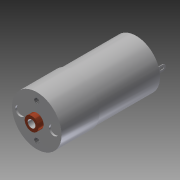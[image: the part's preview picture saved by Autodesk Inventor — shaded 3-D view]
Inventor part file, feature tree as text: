
AUTODESK INVENTOR PART (.ipt)
format: ipt  version: 2014 (Build 180170000, 170)  size: 193,536 bytes
history: native  units: in
note: dims shown in document units (in); Inventor stores cm internally (conversion verified against a paired STEP export)
features: sketch x11, extrude x10, hole x1
ambient origin geometry x8: Origin, YZ Plane, XZ Plane, XY Plane, X Axis, Y Axis, Z Axis, Center Point
bodies: Solid1 (feature_tree)
feature tree (22):
  extrude  "Extrusion1"  Depth=0.74in TaperAngle=0.0deg
  extrude  "Extrusion3"  Depth=0.15in
  hole  "Hole1"  [1 undecoded]
  extrude  "Extrusion4"  Depth=0.11in
  extrude  "Extrusion5"  Depth=1.204in
  extrude  "Extrusion6"  Depth=0.075in
  extrude  "Extrusion7"  Depth=0.075in TaperAngle=0.0deg
  extrude  "Extrusion8"  Depth=0.035in TaperAngle=0.0deg
  extrude  "Extrusion9"  Depth=0.664in
  extrude  "Extrusion10"  Depth=0.034in
  extrude  "Extrusion11"  Depth=0.034in TaperAngle=0.0deg
  sketch  "Sketch1"  dims[d0=0.968in d1=0.74in d2=0.0in]
  sketch  "Sketch2"  dims[d3=0.268in d6=0.15in]
  sketch  "Sketch3"  dims[d7=0.103in d8=0.0in d9=0.675in]
  sketch  "Sketch4"  dims[d10=0.3375in]
  sketch  "Sketch5"  dims[d11=0.097in d12=0.11in d13=0.375in d14=0.25in d15=0.5635in d16=0.11in d17=0.8108in d18=0.934in]
  sketch  "Sketch6"  dims[d19=1.204in d20=0.0in d21=0.324in]
  sketch  "Sketch7"  dims[d22=0.075in d23=0.0in d24=0.142in]
  sketch  "Sketch8"  dims[d25=0.324in d26=0.075in d27=0.0in]
  sketch  "Sketch9"  dims[d28=0.078in d29=0.035in d30=0.0in]
  sketch  "Sketch10"  dims[d31=0.009in d32=0.664in]
  sketch  "Sketch11"  dims[d33=0.119in d34=0.332in d35=0.24in d36=0.0in d37=0.053in d38=0.24in d39=0.0in d41=0.037in d42=0.0229in d45=0.038in d46=0.0229in d47=0.076in d48=0.24in d49=0.0in d50=0.186in d51=0.473in d53=0.659in d54=0.3295in d55=0.034in d56=0.0in]
note: 1 required parameter value undecoded (feature->parameter linkage not recoverable at this tier; creation-order binding heuristic only, values carry confidence <= 0.55)
